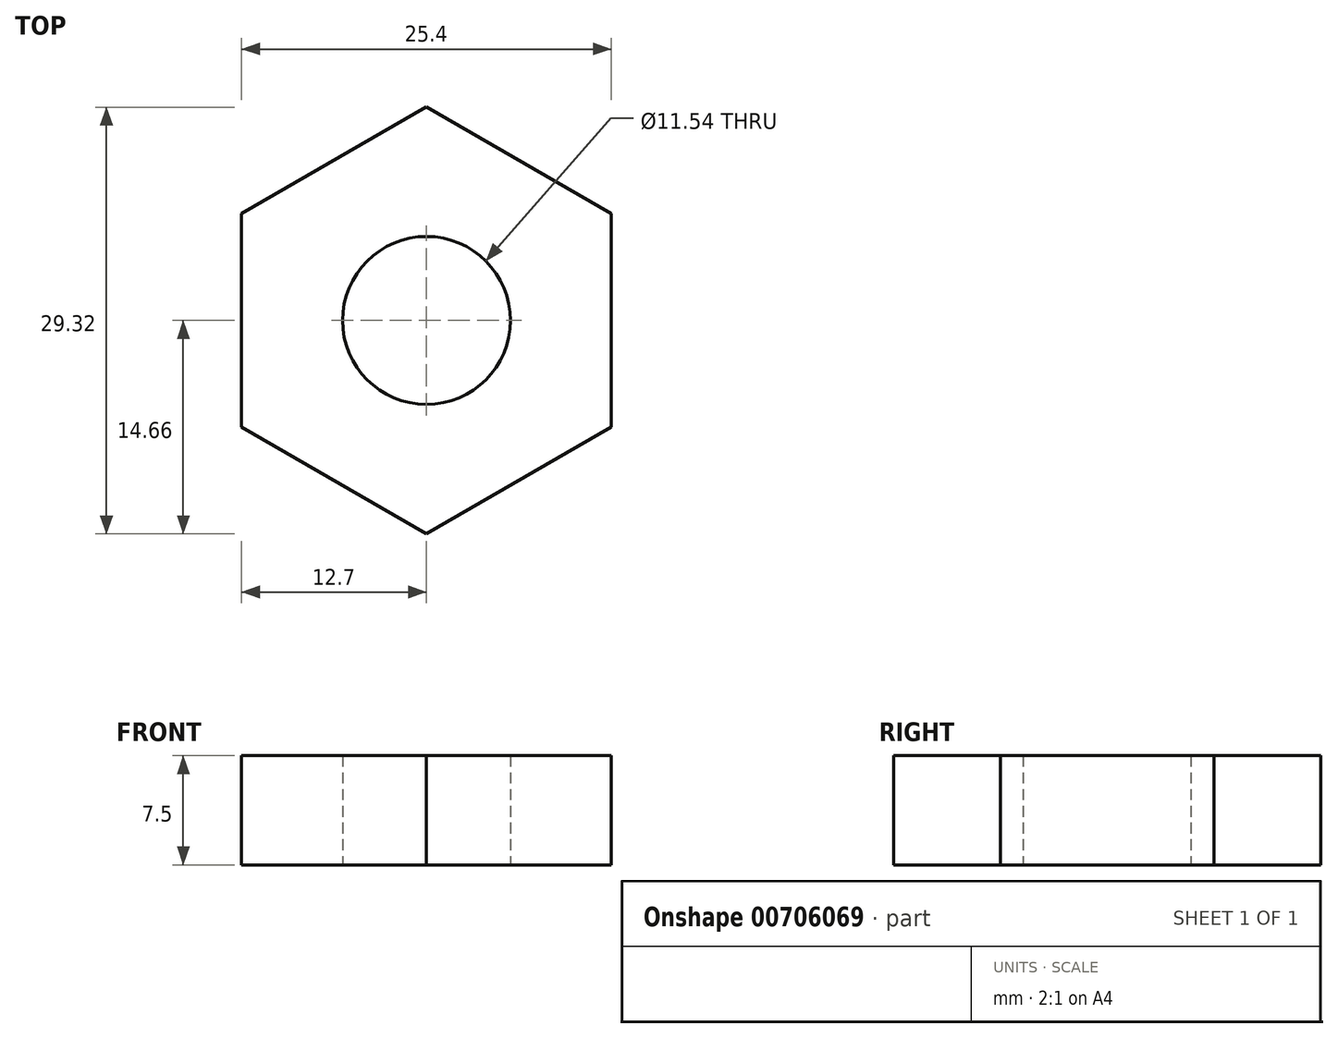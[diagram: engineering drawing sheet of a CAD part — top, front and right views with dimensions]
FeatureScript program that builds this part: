
annotation { "Feature Type Name" : "Feature", "Feature Type Description" : "" }
export const myFeature = defineFeature(function(context is Context, id is Id, definition is map)
    precondition{}
    {
        {
            var Q0;
            Q0=qCreatedBy(makeId("Top.planeOp"),FACE);
            var sketch = newSketch(context, id + "F0", { "sketchPlane" : qUnion([Q0])});
            skCircle(sketch, "E0.cCircle", {"center": v(0, 0) * mm, "radius": 12.7 * mm, "construction": true});
            skLineSegment(sketch, "E0.0", {"start": v(12.7, 7.33) * mm, "end": v(12.7, -7.33) * mm});
            skLineSegment(sketch, "E0.1", {"start": v(12.7, -7.33) * mm, "end": v(0, -14.66) * mm});
            skLineSegment(sketch, "E0.2", {"start": v(0, -14.66) * mm, "end": v(-12.7, -7.33) * mm});
            skLineSegment(sketch, "E0.3", {"start": v(-12.7, -7.33) * mm, "end": v(-12.7, 7.33) * mm});
            skLineSegment(sketch, "E0.4", {"start": v(-12.7, 7.33) * mm, "end": v(0, 14.66) * mm});
            skLineSegment(sketch, "E0.5", {"start": v(0, 14.66) * mm, "end": v(12.7, 7.33) * mm});
            skPoint(sketch, "E0.0.midPoint", {"position": v(12.7, 0) * mm});
            skCircle(sketch, "E1", {"center": v(0, 0) * mm, "radius": 5.77 * mm});
            skSolve(sketch);
        }
        {
            var Q0;
            Q0=makeQuery(id+"F0.imprint","IMPRINT",FACE,{"disambiguationData":[TD([[makeQuery(id+"F0.imprint","IMPRINT",EDGE,{"derivedFrom":sQuery(id+"F0.wireOp",EDGE,"E0.0")}),-1.0]])]});
            extrude(context, id + "F1", {"entities" : qUnion([Q0]), "depth" : 7.5 * mm, "offsetDistance" : 25.4 * mm});
        }
    });
